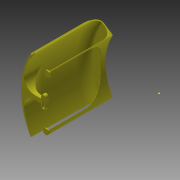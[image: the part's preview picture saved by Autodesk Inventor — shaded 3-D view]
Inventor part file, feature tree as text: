
AUTODESK INVENTOR PART (.ipt)
format: ipt  version: 2015 (Build 190159000, 159)  size: 900,608 bytes
history: native  units: mm
features: sketch x20, extrude x17, fillet x8, revolve x6
ambient origin geometry x8: Origin, YZ Plane, XZ Plane, XY Plane, X Axis, Y Axis, Z Axis, Center Point
bodies: Body1 (feature_tree)
feature tree (51):
  sketch  "Boceto1"  dims[d1=40.0mm d2=20.0mm d3=20.0mm d4=5.0mm d5=360.0deg d6=5.0mm d7=5.0mm d9=5.0mm d10=10.0mm d11=2.451216mm d13=270.0mm]
  revolve  "Revolución1"  [1 undecoded]
  sketch  "Boceto3"  dims[d20=3.0mm d21=120.0mm]
  extrude  "Extrusión2"  Depth=100.0mm
  extrude  "Extrusión3"  Depth=120.0mm
  sketch  "Boceto6"  dims[d22=3.0mm d23=120.0mm]
  revolve  "Revolución2"  [1 undecoded]
  revolve  "Revolución3"  [1 undecoded]
  revolve  "Revolución4"  [1 undecoded]
  revolve  "Revolución5"  [1 undecoded]
  fillet  "Empalme2"  Radius=100.0mm
  sketch  "Boceto7"  dims[d24=90.0deg]
  extrude  "Extrusión7"  Depth=20.0mm
  extrude  "Extrusión8"  Depth=135.0mm
  extrude  "Extrusión9"  TaperAngle=90.0deg  [1 undecoded]
  extrude  "Extrusión10"  TaperAngle=90.0deg  [1 undecoded]
  fillet  "Empalme4"  Radius=3.0mm
  fillet  "Empalme5"  Radius=20.0mm
  sketch  "Boceto16"  dims[d57=135.0mm d58=3.0mm]
  extrude  "Extrusión11"  Depth=10.0mm
  revolve  "Revolución6"  [1 undecoded]
  fillet  "Empalme6"  Radius=8.0mm
  sketch  "Boceto19"  dims[d70=10.0mm d71=10.0mm]
  extrude  "Extrusión12"  Depth=8.0mm
  extrude  "Extrusión13"  Depth=6.0mm TaperAngle=0.0deg
  fillet  "Empalme7"  Radius=20.0mm
  extrude  "Extrusión14"  Depth=6.0mm TaperAngle=0.0deg
  fillet  "Empalme8"  Radius=30.0mm
  fillet  "Empalme9"  Radius=20.0mm
  extrude  "Extrusión15"  TaperAngle=60.0deg  [1 undecoded]
  extrude  "Extrusión16"  TaperAngle=60.0deg  [1 undecoded]
  extrude  "Extrusión17"  Depth=2.0mm
  extrude  "Extrusión18"  Depth=2.0mm
  extrude  "Extrusión19"  Depth=2.0mm
  sketch  "Boceto26"  dims[d101=999.0mm d102=0.0mm d105=2.0mm d106=0.523599mm d107=0.523599mm d108=1.5mm d109=0.5mm d110=999.0mm d111=0.0mm d112=0.523599mm d113=0.523599mm d114=10.0mm d115=0.0mm d116=45.0mm d117=2.0mm d118=0.0mm d119=2.0mm d120=2.0mm d121=3.0mm d122=0.0mm d123=0.5mm d124=0.0mm d125=0.5mm d126=0.0mm d127=2.5mm d128=0.0mm d129=1.5mm d130=0.0mm d131=1.745329mm d132=0.872665mm d133=6.0mm d134=0.0mm d135=6.0mm d136=0.0mm d137=2.0mm]
  extrude  "Extrusión20"  Depth=2.0mm
  extrude  "Extrusión21"  Depth=2.0mm TaperAngle=0.0deg
  fillet  "Empalme10"  Radius=0.523599mm
  sketch  "Boceto2"  dims[d14=3.0mm d19=100.0mm]
  sketch  "Boceto11"  dims[d26=40.0mm d27=20.0mm d28=20.0mm d29=5.0mm d30=360.0deg d31=5.0mm d32=5.0mm d33=5.0mm d34=10.0mm d35=2.451216mm d36=270.0mm d37=3.0mm d38=60.0mm d39=0.0mm]
  sketch  "Boceto12"  dims[d40=3.0mm d41=0.0mm d51=20.0mm]
  sketch  "Boceto13"  dims[d52=45.0mm d53=20.0mm d54=100.0mm]
  sketch  "Boceto14"  dims[d55=90.0deg d56=20.0mm]
  sketch  "Boceto17"  dims[d59=90.0deg d60=90.0deg]
  sketch  "Boceto18"  dims[d61=90.0deg d62=90.0deg d63=3.0mm d69=20.0mm]
  sketch  "Boceto20"  dims[d73=10.0mm d74=111.0mm d75=0.0mm d79=8.0mm]
  sketch  "Boceto21"  dims[d80=8.0mm d81=8.0mm]
  sketch  "Boceto22"  dims[d82=8.0mm d83=6.0mm d84=0.0mm d87=20.0mm d89=360.0deg]
  sketch  "Boceto23"  dims[d91=6.0mm d92=0.0mm d93=6.0mm d94=0.0mm d95=30.0mm d96=20.0mm]
  sketch  "Boceto24"  dims[d97=60.0deg d98=60.0deg]
  sketch  "Boceto25"  dims[d99=60.0deg d100=60.0deg]
note: 10 required parameter values undecoded (feature->parameter linkage not recoverable at this tier; creation-order binding heuristic only, values carry confidence <= 0.55)